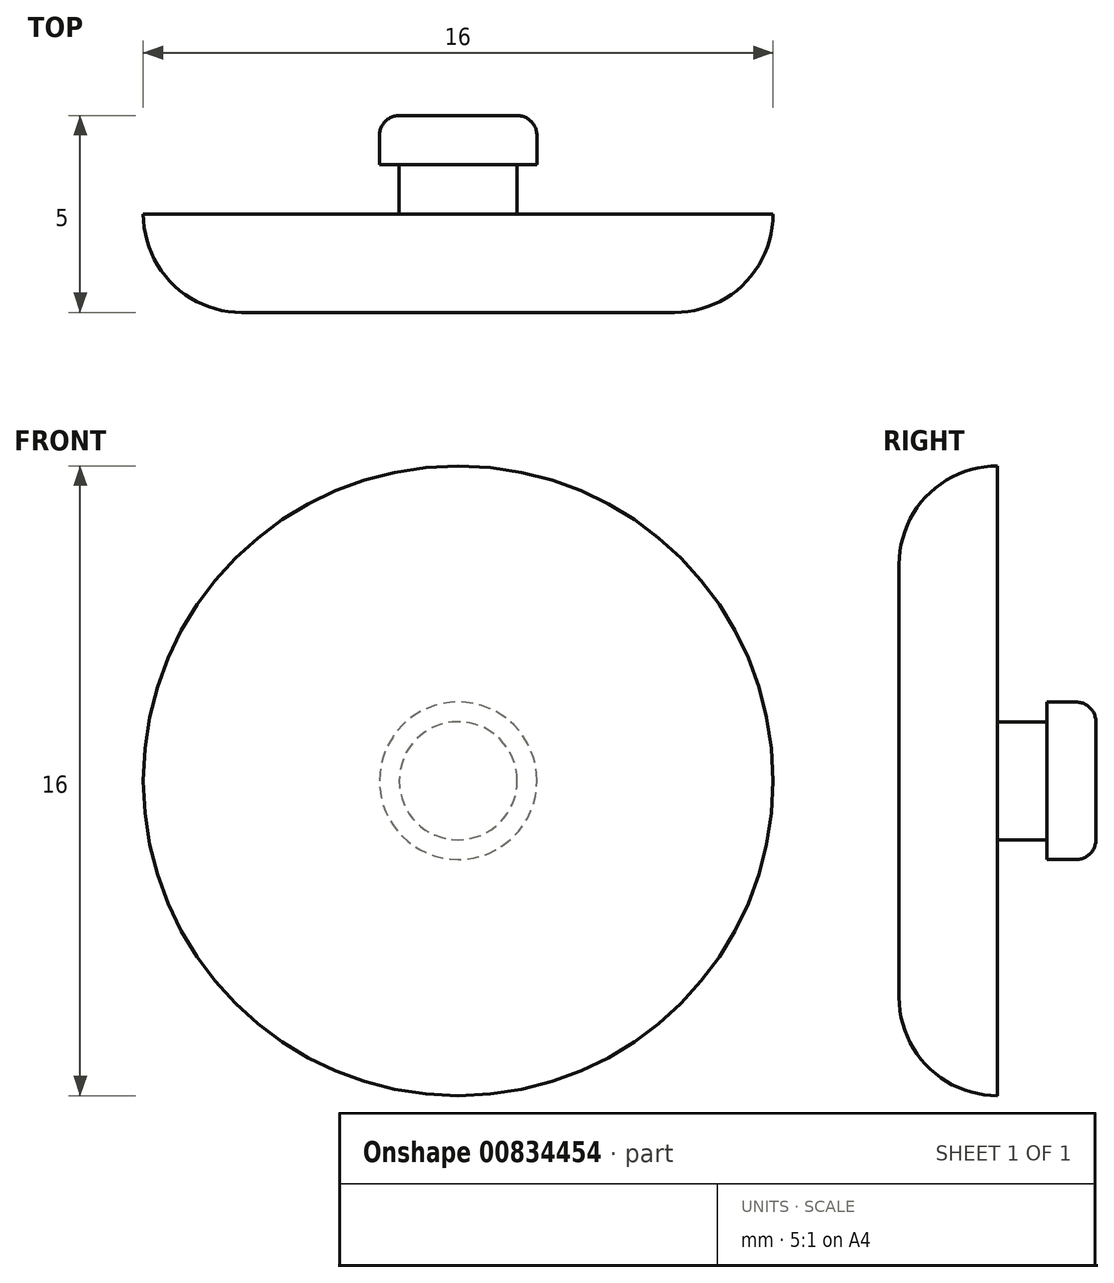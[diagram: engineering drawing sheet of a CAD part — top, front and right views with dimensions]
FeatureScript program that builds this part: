
annotation { "Feature Type Name" : "Feature", "Feature Type Description" : "" }
export const myFeature = defineFeature(function(context is Context, id is Id, definition is map)
    precondition{}
    {
        {
            var Q0;
            Q0=qCreatedBy(makeId("Front.planeOp"),FACE);
            var sketch = newSketch(context, id + "F0", { "sketchPlane" : qUnion([Q0])});
            skCircle(sketch, "E0", {"center": v(0, 0) * mm, "radius": 8 * mm});
            skSolve(sketch);
        }
        {
            var Q0;
            Q0 = qSketchRegion(id + "F0", true);
            extrude(context, id + "F1", {"entities" : qUnion([Q0]), "depth" : 2.5 * mm, "offsetDistance" : 25.4 * mm});
        }
        {
            var Q0;
            Q0=makeQuery(id+"F1.opExtrude","CAP_EDGE",EDGE,{"disambiguationData":[OSD([sQuery(id+"F0.wireOp",EDGE,"E0")])],"isStart":false});
            fillet(context, id + "F2", {"entities" : qUnion([Q0]), "radius" : 2.5 * mm, "tangentPropagation" : true, "allowEdgeOverflow" : false});
        }
        {
            var Q0;
            Q0=qCreatedBy(makeId("Front.planeOp"),FACE);
            var sketch = newSketch(context, id + "F3", { "sketchPlane" : qUnion([Q0])});
            skCircle(sketch, "E1", {"center": v(0, 0) * mm, "radius": 1.5 * mm});
            skSolve(sketch);
        }
        {
            var Q0;
            Q0=makeQuery(id+"F3.imprint","IMPRINT",FACE,{"disambiguationData":[TD([[makeQuery(id+"F3.imprint","IMPRINT",EDGE,{"derivedFrom":sQuery(id+"F3.wireOp",EDGE,"E1")}),1.0]])]});
            var Q1;
            Q1=sQuery(id+"F3.wireOp",EDGE,"E1");
            extrude(context, id + "F4", {"entities" : qUnion([Q0]), "surfaceEntities" : qUnion([Q1]), "oppositeDirection" : true, "depth" : 1.25 * mm, "offsetDistance" : 25.4 * mm});
        }
        {
            var Q0;
            Q0=makeQuery(id+"F4.opExtrude","CAP_FACE",FACE,{"disambiguationData":[OSD([sQuery(id+"F3.wireOp",EDGE,"E1")])],"isStart":false});
            var sketch = newSketch(context, id + "F5", { "sketchPlane" : qUnion([Q0])});
            skCircle(sketch, "E2", {"center": v(0, 0) * mm, "radius": 2 * mm});
            skSolve(sketch);
        }
        {
            var Q0;
            Q0 = qSketchRegion(id + "F5", true);
            extrude(context, id + "F6", {"entities" : qUnion([Q0]), "operationType" : NewBodyOperationType.ADD, "depth" : 1.25 * mm, "offsetDistance" : 25 * mm});
        }
        {
            var Q0;
            Q0=makeQuery(id+"F6.opExtrude","CAP_EDGE",EDGE,{"disambiguationData":[OSD([sQuery(id+"F5.wireOp",EDGE,"E2")])],"isStart":false});
            fillet(context, id + "F7", {"entities" : qUnion([Q0]), "radius" : 0.5 * mm, "tangentPropagation" : true, "allowEdgeOverflow" : false});
        }
    });
